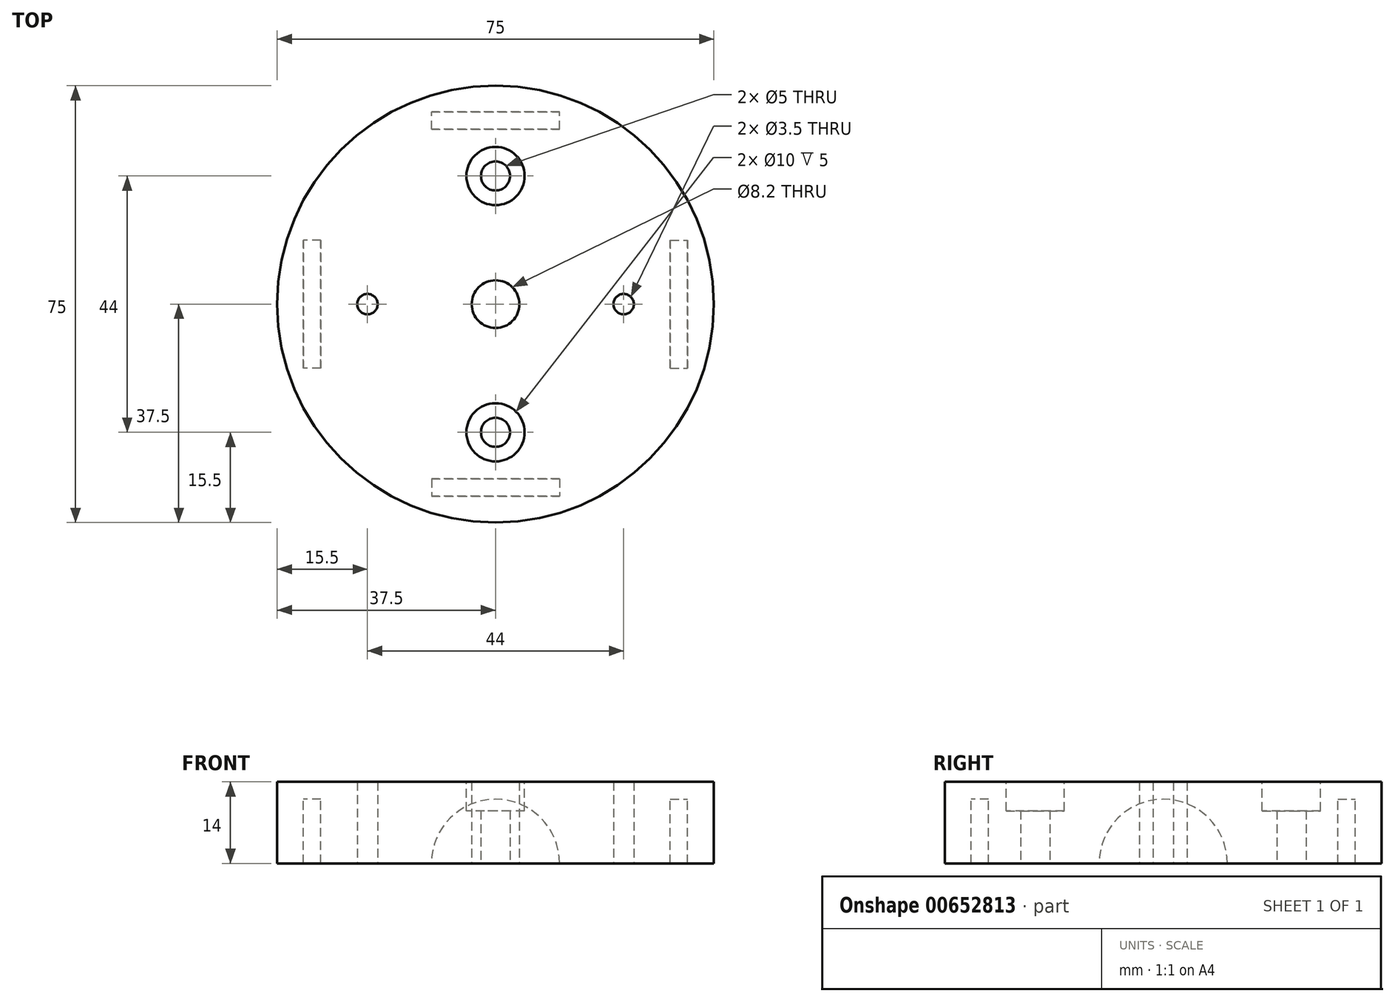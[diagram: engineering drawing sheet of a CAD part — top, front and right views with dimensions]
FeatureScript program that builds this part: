
annotation { "Feature Type Name" : "Feature", "Feature Type Description" : "" }
export const myFeature = defineFeature(function(context is Context, id is Id, definition is map)
    precondition{}
    {
        {
            assignVariable(context, id + "F0", {"name" : "Metal_Diameter", "anyValue" : 22});
        }
        {
            assignVariable(context, id + "F1", {"name" : "Metal_Radius", "anyValue" : 33});
        }
        {
            assignVariable(context, id + "F2", {"name" : "Metal_Thickness", "anyValue" : 3});
        }
        {
            var Q0;
            Q0=qCreatedBy(makeId("Top.planeOp"),FACE);
            var sketch = newSketch(context, id + "F3", { "sketchPlane" : qUnion([Q0])});
            skCircle(sketch, "E0", {"center": v(0, 0) * mm, "radius": 37.5 * mm});
            skCircle(sketch, "E1", {"center": v(0, 0) * mm, "radius": 4.1 * mm});
            skCircle(sketch, "E2", {"center": v(0, 22) * mm, "radius": 2.5 * mm});
            skCircle(sketch, "E3", {"center": v(0, -22) * mm, "radius": 2.5 * mm});
            skCircle(sketch, "E4", {"center": v(22, 0) * mm, "radius": 1.75 * mm});
            skCircle(sketch, "E5", {"center": v(-22, 0) * mm, "radius": 1.75 * mm});
            skSolve(sketch);
        }
        {
            var Q0;
            Q0=makeQuery(id+"F3.imprint","IMPRINT",FACE,{"disambiguationData":[TD([[makeQuery(id+"F3.imprint","IMPRINT",EDGE,{"derivedFrom":sQuery(id+"F3.wireOp",EDGE,"E0")}),1.0]])]});
            extrude(context, id + "F4", {"entities" : qUnion([Q0]), "depth" : (getVariable(context, 'Metal_Diameter') * .5 + 3) * mm, "offsetDistance" : 25 * mm});
        }
        {
            var Q0;
            Q0=qCreatedBy(makeId("Front.planeOp"),FACE);
            cPlane(context, id + "F5", {"entities" : qUnion([Q0]), "cplaneType" : CPlaneType.OFFSET, "offset" : (getVariable(context, 'Metal_Radius')) * mm, "width" : 150 * mm, "height" : 150 * mm});
        }
        {
            var Q0;
            Q0=qCreatedBy(id+"F5.planeOp",FACE);
            var sketch = newSketch(context, id + "F6", { "sketchPlane" : qUnion([Q0])});
            skCircle(sketch, "E6", {"center": v(0, 0) * mm, "radius": 11 * mm});
            skSolve(sketch);
        }
        {
            var Q0;
            Q0=makeQuery(id+"F6.imprint","IMPRINT",FACE,{"disambiguationData":[TD([[makeQuery(id+"F6.imprint","IMPRINT",EDGE,{"derivedFrom":sQuery(id+"F6.wireOp",EDGE,"E6")}),1.0]])]});
            extrude(context, id + "F7", {"entities" : qUnion([Q0]), "operationType" : NewBodyOperationType.REMOVE, "oppositeDirection" : true, "depth" : (getVariable(context, 'Metal_Thickness')) * mm, "offsetDistance" : 25 * mm});
        }
        {
            var Q0;
            Q0=qCreatedBy(makeId("Front.planeOp"),FACE);
            cPlane(context, id + "F8", {"entities" : qUnion([Q0]), "cplaneType" : CPlaneType.OFFSET, "offset" : (getVariable(context, 'Metal_Radius')) * mm, "oppositeDirection" : true, "width" : 150 * mm, "height" : 150 * mm});
        }
        {
            var Q0;
            Q0=qCreatedBy(id+"F8.planeOp",FACE);
            var sketch = newSketch(context, id + "F9", { "sketchPlane" : qUnion([Q0])});
            skCircle(sketch, "E7", {"center": v(0, 0) * mm, "radius": 11 * mm});
            skSolve(sketch);
        }
        {
            var Q0;
            Q0=makeQuery(id+"F9.imprint","IMPRINT",FACE,{"disambiguationData":[TD([[makeQuery(id+"F9.imprint","IMPRINT",EDGE,{"derivedFrom":sQuery(id+"F9.wireOp",EDGE,"E7")}),1.0]])]});
            extrude(context, id + "F10", {"entities" : qUnion([Q0]), "operationType" : NewBodyOperationType.REMOVE, "depth" : (getVariable(context, 'Metal_Thickness')) * mm, "offsetDistance" : 25 * mm});
        }
        {
            var Q0;
            Q0=qCreatedBy(makeId("Right.planeOp"),FACE);
            cPlane(context, id + "F11", {"entities" : qUnion([Q0]), "cplaneType" : CPlaneType.OFFSET, "offset" : (getVariable(context, 'Metal_Radius')) * mm, "width" : 150 * mm, "height" : 150 * mm});
        }
        {
            var Q0;
            Q0=qCreatedBy(makeId("Right.planeOp"),FACE);
            cPlane(context, id + "F12", {"entities" : qUnion([Q0]), "cplaneType" : CPlaneType.OFFSET, "offset" : (getVariable(context, 'Metal_Radius')) * mm, "oppositeDirection" : true, "width" : 150 * mm, "height" : 150 * mm});
        }
        {
            var Q0;
            Q0=qCreatedBy(id+"F11.planeOp",FACE);
            var sketch = newSketch(context, id + "F13", { "sketchPlane" : qUnion([Q0])});
            skCircle(sketch, "E8", {"center": v(0, 0) * mm, "radius": 11 * mm});
            skSolve(sketch);
        }
        {
            var Q0;
            Q0=makeQuery(id+"F13.imprint","IMPRINT",FACE,{"disambiguationData":[TD([[makeQuery(id+"F13.imprint","IMPRINT",EDGE,{"derivedFrom":sQuery(id+"F13.wireOp",EDGE,"E8")}),1.0]])]});
            extrude(context, id + "F14", {"entities" : qUnion([Q0]), "operationType" : NewBodyOperationType.REMOVE, "oppositeDirection" : true, "depth" : (getVariable(context, 'Metal_Thickness')) * mm, "offsetDistance" : 25 * mm});
        }
        {
            var Q0;
            Q0=qCreatedBy(id+"F12.planeOp",FACE);
            var sketch = newSketch(context, id + "F15", { "sketchPlane" : qUnion([Q0])});
            skCircle(sketch, "E9", {"center": v(0, 0) * mm, "radius": 11 * mm});
            skSolve(sketch);
        }
        {
            var Q0;
            Q0=makeQuery(id+"F15.imprint","IMPRINT",FACE,{"disambiguationData":[TD([[makeQuery(id+"F15.imprint","IMPRINT",EDGE,{"derivedFrom":sQuery(id+"F15.wireOp",EDGE,"E9")}),1.0]])]});
            extrude(context, id + "F16", {"entities" : qUnion([Q0]), "operationType" : NewBodyOperationType.REMOVE, "depth" : (getVariable(context, 'Metal_Thickness')) * mm, "offsetDistance" : 25 * mm});
        }
        {
            var Q0;
            Q0=makeQuery(id+"F4.opExtrude","CAP_FACE",FACE,{"disambiguationData":[OSD([sQuery(id+"F3.wireOp",EDGE,"E0"),sQuery(id+"F3.wireOp",EDGE,"E1"),sQuery(id+"F3.wireOp",EDGE,"E2"),sQuery(id+"F3.wireOp",EDGE,"E3"),sQuery(id+"F3.wireOp",EDGE,"E4"),sQuery(id+"F3.wireOp",EDGE,"E5")])],"isStart":false});
            cPlane(context, id + "F17", {"entities" : qUnion([Q0]), "cplaneType" : CPlaneType.OFFSET, "offset" : 0 * mm, "width" : 150 * mm, "height" : 150 * mm});
        }
        {
            var Q0;
            Q0=qCreatedBy(id+"F17.planeOp",FACE);
            var sketch = newSketch(context, id + "F18", { "sketchPlane" : qUnion([Q0])});
            skCircle(sketch, "E10", {"center": v(0, 22) * mm, "radius": 5 * mm});
            skCircle(sketch, "E11", {"center": v(0, -22) * mm, "radius": 5 * mm});
            skSolve(sketch);
        }
        {
            var Q0;
            Q0=makeQuery(id+"F18.imprint","IMPRINT",FACE,{"disambiguationData":[TD([[makeQuery(id+"F18.imprint","IMPRINT",EDGE,{"derivedFrom":sQuery(id+"F18.wireOp",EDGE,"4dBqTVrm-y3i4-cTxl-pwbQ-dSN0dZ4WlPbn")}),1.0]])]});
            var Q1;
            Q1=makeQuery(id+"F18.imprint","IMPRINT",FACE,{"disambiguationData":[TD([[makeQuery(id+"F18.imprint","IMPRINT",EDGE,{"derivedFrom":sQuery(id+"F18.wireOp",EDGE,"E10")}),1.0]])]});
            var Q2;
            Q2=makeQuery(id+"F18.imprint","IMPRINT",FACE,{"disambiguationData":[TD([[makeQuery(id+"F18.imprint","IMPRINT",EDGE,{"derivedFrom":sQuery(id+"F18.wireOp",EDGE,"4mraNu2k-Mp4V-bzQi-bqZU-Ab9iPvHCnPMr")}),1.0]])]});
            var Q3;
            Q3=makeQuery(id+"F18.imprint","IMPRINT",FACE,{"disambiguationData":[TD([[makeQuery(id+"F18.imprint","IMPRINT",EDGE,{"derivedFrom":sQuery(id+"F18.wireOp",EDGE,"E11")}),1.0]])]});
            extrude(context, id + "F19", {"entities" : qUnion([Q0, Q1, Q2, Q3]), "operationType" : NewBodyOperationType.REMOVE, "oppositeDirection" : true, "depth" : 5 * mm, "offsetDistance" : 25 * mm});
        }
    });
